# Revit family: NXRC
name_source: partatom
category: Communication Devices
revit_build: Autodesk Revit 2014 (Build: 20130308_1515(x64)
units: mm (PartAtom-declared; Revit-internal decimal feet)

## types (1)
- NXRC
    Assembly Code = D5090
    Certification = Conforms with UL916 and Certified to CAN/CSA C22.2 No. 205-M1983
IC Approved
Title 24 compliance
    Controls - Intergral Sensors = NX Occupancy Sensors, Daylight Sensors and Smart Switch Stations
    Default Elevation = 48 "
    Description = The NX Room Controller is the central component of the NX room control solution. Used individually or in combination with other NX Room Controllers, the NX Room Controller provides a complete standalone room control solution that can be networked for facility wide lighting control. The NX Room Controller uses SmartPORT technology to automatically configure occupancy sensors and manual control switches to provide an energy efficient room control solution without the need for any programming or commissioning. When devices are plugged into one of the NX Room Controllers SmartPORTs, the NX Room Controller automatically and intelligently configures the connected devices for operation. Changes may be made to the automatic configurations at any time using NX Bluetooth enabled Apps or when networked through the NX Area Controller. NX Room Controllers are available with one or two independently controlled relays for On/Off and Bi-Level control. Dimming versions are available with one or two 0-10V control signal outputs for full range dimming control of dimmable ballasts and LED drivers.
    Dimming = Class 2 0-10VDC, 60mA per channel
For use with low voltage, two-wire dimming ballast and LED drivers
    Features = Single or dual relay versions for On/Off or bi-level control
Approved for use with controlled receptacles
Optional 0-10V interface for full range dimming control
Override push button and status LED per relay/dimmer
SmartPORT auto configuration support for NX Occupancy Sensors, Daylight Sensors and Smart Switch Stations
Advanced wireless Bluetooth configuration with free iOS and Android Apps
Intelligently and automatically responds to sensors and switches in the most energy efficient manner
Connect NX Room Controllers with CAT5 for additional loads
Schedules are held in the devices themselves (requires optional network connection)
UL Listed
Five-year limited warranty
    Housing Material = Plastic - Hubbell - Blue
    L = 5.26 "
    Manufacturer = Hubbell Control Solutions
    Model = NX Room Controller
    Product Documentation Link = https://hubbellcdn.com
    Product Page URL = https://www.hubbell.com
    Standby Power = 120VAC: 1.2,277VAC: 1.5,347VAC: 1.5
    Type Comments = NX Room Controller
    URL = https://www.hubbell.com
    Voltage = 120/277/347 VAC
    Warranty = 5-Years Warranty
    Washer = Metal-Hubbell-Galvanized_Steel

## geometry (parser evidence)
native form markers: Sweep x1
no freeform markers — native parametric forms only
